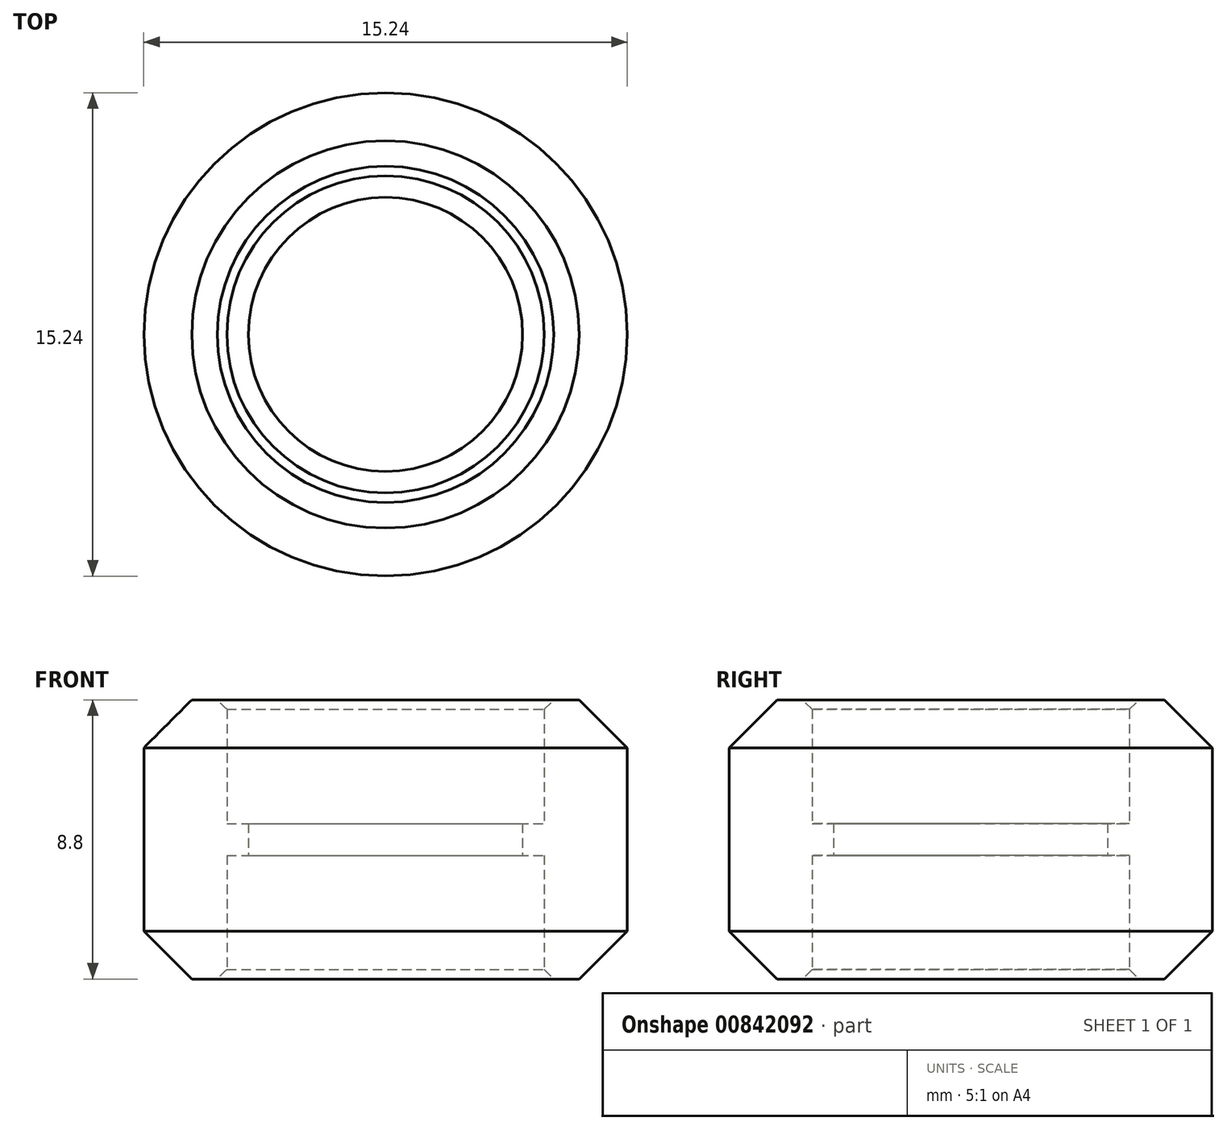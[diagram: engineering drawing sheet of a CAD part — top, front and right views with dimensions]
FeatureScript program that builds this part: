
annotation { "Feature Type Name" : "Feature", "Feature Type Description" : "" }
export const myFeature = defineFeature(function(context is Context, id is Id, definition is map)
    precondition{}
    {
        {
            var Q0;
            Q0=qCreatedBy(makeId("Front.planeOp"),FACE);
            var sketch = newSketch(context, id + "F0", { "sketchPlane" : qUnion([Q0])});
            skLineSegment(sketch, "E0", {"start": v(-5.3, 4.4) * mm, "end": v(-6.1, 4.4) * mm});
            skLineSegment(sketch, "E1", {"start": v(-6.1, 4.4) * mm, "end": v(-7.62, 2.89) * mm});
            skLineSegment(sketch, "E2", {"start": v(-7.62, 2.89) * mm, "end": v(-7.61, -2.9) * mm});
            skLineSegment(sketch, "E3", {"start": v(-7.61, -2.9) * mm, "end": v(-6.1, -4.4) * mm});
            skLineSegment(sketch, "E4", {"start": v(-6.1, -4.4) * mm, "end": v(-5.3, -4.4) * mm});
            skLineSegment(sketch, "E5", {"start": v(-5, 4.1) * mm, "end": v(-5, 0.5) * mm});
            skLineSegment(sketch, "E6", {"start": v(-5, 0.5) * mm, "end": v(-4.32, 0.5) * mm});
            skLineSegment(sketch, "E7", {"start": v(-4.32, 0.5) * mm, "end": v(-4.32, -0.5) * mm});
            skLineSegment(sketch, "E8", {"start": v(-4.32, -0.5) * mm, "end": v(-5, -0.5) * mm});
            skLineSegment(sketch, "E9", {"start": v(-5, -0.5) * mm, "end": v(-5, -4.1) * mm});
            skLineSegment(sketch, "E10", {"start": v(-5.3, 4.4) * mm, "end": v(-5, 4.1) * mm});
            skLineSegment(sketch, "E11.MirrorCS", {"start": v(-5.3, -4.4) * mm, "end": v(-5, -4.1) * mm});
            skLineSegment(sketch, "E12", {"start": v(0, 0) * mm, "end": v(-2.59, 0) * mm, "construction": true});
            skLineSegment(sketch, "E13", {"start": v(0, -4.4) * mm, "end": v(0, 4.4) * mm, "construction": true});
            skPoint(sketch, "E14", {"position": v(-4.32, 0) * mm});
            skSolve(sketch);
        }
        {
            var Q0;
            Q0=makeQuery(id+"F0.imprint","IMPRINT",FACE,{"disambiguationData":[TD([[makeQuery(id+"F0.imprint","IMPRINT",EDGE,{"derivedFrom":sQuery(id+"F0.wireOp",EDGE,"E0")}),1.0]])]});
            var Q1;
            Q1=sQuery(id+"F0.wireOp",EDGE,"E13");
            revolve(context, id + "F1", {"surfaceOperationType" : NewSurfaceOperationType.NEW, "entities" : qUnion([Q0]), "axis" : qUnion([Q1]), "revolveType" : RevolveType.FULL});
        }
        {
            var Q0;
            Q0=qSketchRegion(id+"F0",true);
            var Q1;
            Q1=sQuery(id+"F0.wireOp",EDGE,"E13");
            revolve(context, id + "F2", {"surfaceOperationType" : NewSurfaceOperationType.NEW, "entities" : qUnion([Q0]), "axis" : qUnion([Q1]), "revolveType" : RevolveType.FULL});
        }
    });
